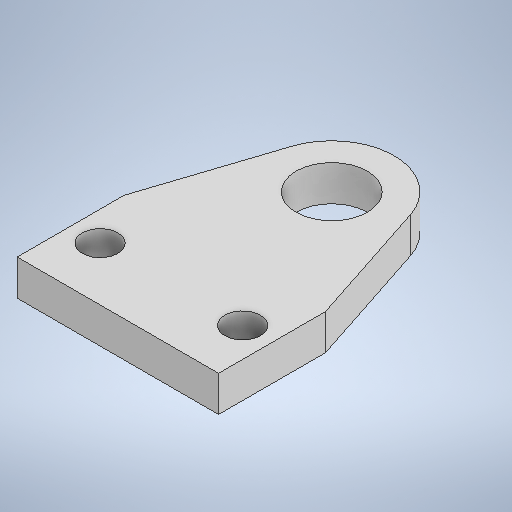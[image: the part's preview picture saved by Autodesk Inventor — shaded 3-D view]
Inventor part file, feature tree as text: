
AUTODESK INVENTOR PART (.ipt)
format: ipt  version: 2025.1 (Build 291241000, 241)  size: 246,272 bytes
history: native  units: mm
features: extrude x1, sketch x1
ambient origin geometry x8: Origin, YZ Plane, XZ Plane, XY Plane, X Axis, Y Axis, Z Axis, Center Point
bodies: Solid1 (feature_tree)
feature tree (2):
  extrude  "Extrusion1"  Depth=11.3mm
  sketch  "Sketch1"  dims[d0=3.5mm d1=6.0mm d2=12.0mm d3=3.0mm d4=4.0mm d5=8.0mm d6=2.0mm d7=4.0mm d8=2.0mm d9=0.0mm d10=11.3mm]
